FCSTD DOCUMENT  (FreeCAD 0.16R6710 (Git))
Label: body
License: All rights reserved
LicenseURL: http://en.wikipedia.org/wiki/All_rights_reserved
objects: Sketcher::SketchObject×1
note: 1 computed .brp shape members not serialized (recipe doc carries the construction recipe); baked Part::Feature solids carry a one-line shape summary decoded from their .brp

FEATURE [Sketcher::SketchObject] Sketch  label="body"
  sketch-geometry (89):
    g0: LineSegment [constr] StartX=205.497 StartY=-4.89478 StartZ=0 EndX=205.497 EndY=-171.461 EndZ=0
    g1: GeomPoint [constr] X=205.497 Y=-88.1781 Z=0
    g2: GeomPoint [constr] X=255.497 Y=-88.1781 Z=0
    g3: LineSegment StartX=258.497 StartY=-82.2781 StartZ=0 EndX=280.997 EndY=-82.2781 EndZ=0
    g4: LineSegment StartX=280.997 StartY=-82.2781 StartZ=0 EndX=280.997 EndY=-94.0781 EndZ=0
    g5: LineSegment StartX=280.997 StartY=-94.0781 StartZ=0 EndX=258.497 EndY=-94.0781 EndZ=0
    g6: LineSegment StartX=258.497 StartY=-94.0781 StartZ=0 EndX=258.497 EndY=-82.2781 EndZ=0
    g7: Circle CenterX=283.997 CenterY=-88.1781 CenterZ=0 NormalX=0 NormalY=0 NormalZ=1 Radius=1.2
    g8: Circle CenterX=255.497 CenterY=-88.1781 CenterZ=0 NormalX=0 NormalY=0 NormalZ=1 Radius=1.2
    g9: GeomPoint [constr] X=275.097 Y=-88.1781 Z=0
    g10: LineSegment [constr] StartX=135.897 StartY=-88.1781 StartZ=0 EndX=275.097 EndY=-88.1781 EndZ=0
    g11: GeomPoint [constr] X=155.497 Y=-88.1781 Z=0
    g12: LineSegment StartX=152.497 StartY=-94.0781 StartZ=0 EndX=129.997 EndY=-94.0781 EndZ=0
    g13: LineSegment StartX=129.997 StartY=-94.0781 StartZ=0 EndX=129.997 EndY=-82.2781 EndZ=0
    g14: LineSegment StartX=129.997 StartY=-82.2781 StartZ=0 EndX=152.497 EndY=-82.2781 EndZ=0
    g15: LineSegment StartX=152.497 StartY=-82.2781 StartZ=0 EndX=152.497 EndY=-94.0781 EndZ=0
    g16: Circle CenterX=126.997 CenterY=-88.1781 CenterZ=0 NormalX=0 NormalY=0 NormalZ=1 Radius=1.2
    g17: Circle CenterX=155.497 CenterY=-88.1781 CenterZ=0 NormalX=0 NormalY=0 NormalZ=1 Radius=1.2
    g18: GeomPoint [constr] X=135.897 Y=-88.1781 Z=0
    g19: GeomPoint [constr] X=205.497 Y=-31.8304 Z=0
    g20: GeomPoint [constr] X=205.497 Y=-144.526 Z=0
    g21: LineSegment [constr] StartX=205.497 StartY=-31.8304 StartZ=0 EndX=263.261 EndY=-4.89478 EndZ=0
    g22: LineSegment [constr] StartX=263.261 StartY=-4.89478 StartZ=0 EndX=147.733 EndY=-4.89478 EndZ=0
    g23: GeomPoint [constr] X=205.497 Y=-4.89478 Z=0
    g24: GeomPoint [constr] X=245.497 Y=-13.1781 Z=0
    g25: LineSegment StartX=245.723 StartY=-6.56303 StartZ=0 EndX=266.115 EndY=2.94588 EndZ=0
    g26: LineSegment StartX=266.115 StartY=2.94588 StartZ=0 EndX=271.101 EndY=-7.74855 EndZ=0
    g27: LineSegment StartX=271.101 StartY=-7.74855 StartZ=0 EndX=250.709 EndY=-17.2575 EndZ=0
    g28: LineSegment StartX=250.709 StartY=-17.2575 StartZ=0 EndX=245.723 EndY=-6.56303 EndZ=0
    g29: Circle CenterX=271.327 CenterY=-1.13348 CenterZ=0 NormalX=0 NormalY=0 NormalZ=1 Radius=1.2
    g30: Circle CenterX=245.497 CenterY=-13.1781 CenterZ=0 NormalX=0 NormalY=0 NormalZ=1 Radius=1.2
    g31: GeomPoint [constr] X=263.261 Y=-4.89478 Z=0
    g32: LineSegment [constr] StartX=205.497 StartY=-31.8304 StartZ=0 EndX=147.733 EndY=-4.89478 EndZ=0
    g33: GeomPoint [constr] X=165.497 Y=-13.1781 Z=0
    g34: LineSegment StartX=160.285 StartY=-17.2575 StartZ=0 EndX=139.893 EndY=-7.74855 EndZ=0
    g35: LineSegment StartX=139.893 StartY=-7.74855 StartZ=0 EndX=144.88 EndY=2.94588 EndZ=0
    g36: LineSegment StartX=144.88 StartY=2.94588 StartZ=0 EndX=165.272 EndY=-6.56303 EndZ=0
    g37: LineSegment StartX=165.272 StartY=-6.56303 StartZ=0 EndX=160.285 EndY=-17.2575 EndZ=0
    g38: Circle CenterX=139.667 CenterY=-1.13348 CenterZ=0 NormalX=0 NormalY=0 NormalZ=1 Radius=1.2
    g39: Circle CenterX=165.497 CenterY=-13.1781 CenterZ=0 NormalX=0 NormalY=0 NormalZ=1 Radius=1.2
    g40: GeomPoint [constr] X=147.733 Y=-4.89478 Z=0
    g41: LineSegment [constr] StartX=263.261 StartY=-4.89478 StartZ=0 EndX=263.261 EndY=-171.461 EndZ=0
    g42: GeomPoint [constr] X=263.261 Y=-88.1781 Z=0
    g43: LineSegment [constr] StartX=205.497 StartY=-144.526 StartZ=0 EndX=263.261 EndY=-171.461 EndZ=0
    g44: LineSegment [constr] StartX=205.497 StartY=-144.526 StartZ=0 EndX=147.733 EndY=-171.461 EndZ=0
    g45: LineSegment StartX=271.101 StartY=-168.608 StartZ=0 EndX=266.115 EndY=-179.302 EndZ=0
    g46: Circle CenterX=271.327 CenterY=-175.223 CenterZ=0 NormalX=0 NormalY=0 NormalZ=1 Radius=1.2
    g47: GeomPoint [constr] X=263.261 Y=-171.461 Z=0
    g48: GeomPoint [constr] X=245.497 Y=-163.178 Z=0
    g49: LineSegment StartX=250.709 StartY=-159.099 StartZ=0 EndX=271.101 EndY=-168.608 EndZ=0
    g50: LineSegment StartX=266.115 StartY=-179.302 StartZ=0 EndX=245.723 EndY=-169.793 EndZ=0
    g51: LineSegment StartX=245.723 StartY=-169.793 StartZ=0 EndX=250.709 EndY=-159.099 EndZ=0
    g52: Circle CenterX=245.497 CenterY=-163.178 CenterZ=0 NormalX=0 NormalY=0 NormalZ=1 Radius=1.2
    g53: LineSegment StartX=144.88 StartY=-179.302 StartZ=0 EndX=139.893 EndY=-168.608 EndZ=0
    g54: Circle CenterX=139.667 CenterY=-175.223 CenterZ=0 NormalX=0 NormalY=0 NormalZ=1 Radius=1.2
    g55: GeomPoint [constr] X=147.733 Y=-171.461 Z=0
    g56: GeomPoint [constr] X=165.497 Y=-163.178 Z=0
    g57: LineSegment StartX=165.272 StartY=-169.793 StartZ=0 EndX=144.88 EndY=-179.302 EndZ=0
    g58: LineSegment StartX=139.893 StartY=-168.608 StartZ=0 EndX=160.285 EndY=-159.099 EndZ=0
    g59: LineSegment StartX=160.285 StartY=-159.099 StartZ=0 EndX=165.272 EndY=-169.793 EndZ=0
    g60: Circle CenterX=165.497 CenterY=-163.178 CenterZ=0 NormalX=0 NormalY=0 NormalZ=1 Radius=1.2
    g61: ArcOfCircle CenterX=263.261 CenterY=-4.89478 CenterZ=0 NormalX=0 NormalY=0 NormalZ=1 Radius=13 StartAngle=5.14872 EndAngle=8.29031
    g62: ArcOfCircle CenterX=275.097 CenterY=-88.1781 CenterZ=0 NormalX=0 NormalY=0 NormalZ=1 Radius=13 StartAngle=4.71239 EndAngle=7.85398
    g63: LineSegment [constr] StartX=275.097 StartY=-88.1781 StartZ=0 EndX=288.683 EndY=-82.3075 EndZ=0
    g64: LineSegment [constr] StartX=288.683 StartY=-82.3075 StartZ=0 EndX=287.497 EndY=-96.2572 EndZ=0
    g65: LineSegment [constr] StartX=287.497 StartY=-96.2572 StartZ=0 EndX=275.097 EndY=-88.1781 EndZ=0
    g66: GeomPoint [constr] X=288.09 Y=-89.2824 Z=0
    g67: LineSegment [constr] StartX=275.097 StartY=-88.1781 StartZ=0 EndX=308.018 EndY=-90.976 EndZ=0
    g68: LineSegment [constr] StartX=257.767 StartY=6.88722 StartZ=0 EndX=268.755 EndY=-16.6768 EndZ=0
    g69: LineSegment [constr] StartX=275.097 StartY=-75.1781 StartZ=0 EndX=275.097 EndY=-101.178 EndZ=0
    g70: LineSegment [constr] StartX=263.261 StartY=-4.89478 StartZ=0 EndX=276.573 EndY=1.57163 EndZ=0
    g71: LineSegment [constr] StartX=276.573 StartY=1.57163 StartZ=0 EndX=276.007 EndY=-12.4169 EndZ=0
    g72: LineSegment [constr] StartX=276.007 StartY=-12.4169 StartZ=0 EndX=263.261 EndY=-4.89478 EndZ=0
    g73: GeomPoint [constr] X=276.29 Y=-5.42263 Z=0
    g74: LineSegment [constr] StartX=263.261 StartY=-4.89478 StartZ=0 EndX=296.274 EndY=-6.23222 EndZ=0
    g75: ArcOfCircle CenterX=263.261 CenterY=-171.461 CenterZ=0 NormalX=0 NormalY=0 NormalZ=1 Radius=13 StartAngle=4.27606 EndAngle=7.41765
    g76: LineSegment [constr] StartX=268.755 StartY=-159.679 StartZ=0 EndX=257.767 EndY=-183.243 EndZ=0
    g77: ArcOfCircle CenterX=147.733 CenterY=-171.461 CenterZ=0 NormalX=0 NormalY=0 NormalZ=1 Radius=13 StartAngle=2.00713 EndAngle=5.14872
    g78: ArcOfCircle CenterX=135.897 CenterY=-88.1781 CenterZ=0 NormalX=0 NormalY=0 NormalZ=1 Radius=13 StartAngle=1.5708 EndAngle=4.71239
    g79: ArcOfCircle CenterX=147.733 CenterY=-4.89478 CenterZ=0 NormalX=0 NormalY=0 NormalZ=1 Radius=13 StartAngle=1.13446 EndAngle=4.27606
    g80: LineSegment [constr] StartX=142.239 StartY=-159.679 StartZ=0 EndX=153.228 EndY=-183.243 EndZ=0
    g81: LineSegment [constr] StartX=135.897 StartY=-75.1781 StartZ=0 EndX=135.897 EndY=-101.178 EndZ=0
    g82: LineSegment [constr] StartX=153.228 StartY=6.88722 StartZ=0 EndX=142.239 EndY=-16.6768 EndZ=0
    g83: ArcOfCircle CenterX=275.098 CenterY=-45.5836 CenterZ=0 NormalX=0 NormalY=0 NormalZ=1 Radius=29.5945 StartAngle=1.78679 EndAngle=4.71238
    g84: ArcOfCircle CenterX=275.098 CenterY=-130.773 CenterZ=0 NormalX=0 NormalY=0 NormalZ=1 Radius=29.5945 StartAngle=1.57081 EndAngle=4.49639
    g85: ArcOfCircle CenterX=135.897 CenterY=-130.773 CenterZ=0 NormalX=0 NormalY=0 NormalZ=1 Radius=29.5945 StartAngle=4.92839 EndAngle=7.85397
    g86: ArcOfCircle CenterX=135.897 CenterY=-45.5836 CenterZ=0 NormalX=0 NormalY=0 NormalZ=1 Radius=29.5945 StartAngle=4.7124 EndAngle=7.63798
    g87: ArcOfCircle CenterX=205.497 CenterY=118.979 CenterZ=0 NormalX=0 NormalY=0 NormalZ=1 Radius=123.68 StartAngle=4.27606 EndAngle=5.14872
    g88: ArcOfCircle CenterX=205.497 CenterY=-295.335 CenterZ=0 NormalX=0 NormalY=0 NormalZ=1 Radius=123.68 StartAngle=1.13446 EndAngle=2.00713
  constraints (226):
    c: Vertical(g0)
    c: Symmetric(g0,g0,g1)
    c: Coincident(g3,g4)
    c: Coincident(g4,g5)
    c: Coincident(g5,g6)
    c: Coincident(g6,g3)
    c: Distance(g4,g3) = 11.8
    c: Distance(g4,g6) = 22.5
    c: Perpendicular(g6,g3)
    c: Perpendicular(g6,g5)
    c: Perpendicular(g4,g5)
    c: Distance(g7,g4) = 3
    c: Distance(g7,g3) = 5.9
    c: Distance(g8,g3) = 5.9
    c: Distance(g8,g6) = 3
    c: Coincident(g2,g8)
    c: Distance(g9,g4) = 5.9
    c: Distance(g9,g3) = 5.9
    c: Horizontal(g10)
    c: Symmetric(g10,g10,g1)
    c: Coincident(g9,g10)
    c: PointOnObject(g2,g10)
    c: Coincident(g12,g13)
    c: Coincident(g13,g14)
    c: Coincident(g14,g15)
    c: Coincident(g15,g12)
    c: Distance(g13,g12) = 11.8
    c: Distance(g13,g15) = 22.5
    c: Perpendicular(g15,g12)
    c: Perpendicular(g15,g14)
    c: Perpendicular(g13,g14)
    c: Distance(g16,g13) = 3
    c: Distance(g16,g12) = 5.9
    c: Distance(g17,g12) = 5.9
    c: Distance(g17,g15) = 3
    c: Coincident(g11,g17)
    c: Distance(g18,g13) = 5.9
    c: Distance(g18,g12) = 5.9
    c: Coincident(g10,g18)
    c: PointOnObject(g11,g10)
    c: PointOnObject(g19,g0)
    c: Symmetric(g20,g19,g1)
    c: Coincident(g21,g19)
    c: Coincident(g22,g21)
    c: Horizontal(g22)
    c: PointOnObject(g23,g22)
    c: PointOnObject(g23,g0)
    c: Symmetric(g21,g22,g23)
    c: Coincident(g25,g26)
    c: Coincident(g26,g27)
    c: Coincident(g27,g28)
    c: Coincident(g28,g25)
    c: Distance(g26,g25) = 11.8
    c: Distance(g26,g28) = 22.5
    c: Perpendicular(g28,g25)
    c: Perpendicular(g28,g27)
    c: Perpendicular(g26,g27)
    c: Distance(g29,g26) = 3
    c: Distance(g29,g25) = 5.9
    c: Distance(g30,g25) = 5.9
    c: Distance(g30,g28) = 3
    c: Coincident(g24,g30)
    c: Distance(g31,g26) = 5.9
    c: Distance(g31,g25) = 5.9
    c: Coincident(g21,g31)
    c: PointOnObject(g24,g21)
    c: Coincident(g32,g19)
    c: Coincident(g32,g22)
    c: Coincident(g34,g35)
    c: Coincident(g35,g36)
    c: Coincident(g36,g37)
    c: Coincident(g37,g34)
    c: Distance(g35,g34) = 11.8
    c: Distance(g35,g37) = 22.5
    c: Perpendicular(g37,g34)
    c: Perpendicular(g37,g36)
    c: Perpendicular(g35,g36)
    c: Distance(g38,g35) = 3
    c: Distance(g38,g34) = 5.9
    c: Distance(g39,g34) = 5.9
    c: Distance(g39,g37) = 3
    c: Coincident(g33,g39)
    c: Distance(g40,g35) = 5.9
    c: Distance(g40,g34) = 5.9
    c: Coincident(g22,g40)
    c: PointOnObject(g33,g32)
    c: Vertical(g41)
    c: Coincident(g21,g41)
    c: PointOnObject(g42,g41)
    c: PointOnObject(g42,g10)
    c: Symmetric(g21,g41,g42)
    c: PointOnObject(g0,g22)
    c: Radius(g7) = 1.2
    c: Radius(g8) = 1.2
    c: Radius(g29) = 1.2
    c: Radius(g30) = 1.2
    c: Radius(g38) = 1.2
    c: Radius(g39) = 1.2
    c: Radius(g17) = 1.2
    c: Radius(g16) = 1.2
    c: Coincident(g43,g20)
    c: Coincident(g43,g41)
    c: Coincident(g44,g20)
    c: Symmetric(g41,g44,g0)
    c: Coincident(g49,g45)
    c: Coincident(g45,g50)
    c: Coincident(g50,g51)
    c: Coincident(g51,g49)
    c: Distance(g45,g49) = 11.8
    c: Distance(g45,g51) = 22.5
    c: Perpendicular(g51,g49)
    c: Perpendicular(g51,g50)
    c: Perpendicular(g45,g50)
    c: Distance(g46,g45) = 3
    c: Distance(g46,g49) = 5.9
    c: Distance(g52,g49) = 5.9
    c: Distance(g52,g51) = 3
    c: Coincident(g48,g52)
    c: Distance(g47,g45) = 5.9
    c: Distance(g47,g49) = 5.9
    c: Equal(g7,g46) = 1.2
    c: Equal(g8,g52) = 1.2
    c: Coincident(g41,g47)
    c: PointOnObject(g48,g43)
    c: Coincident(g57,g53)
    c: Coincident(g53,g58)
    c: Coincident(g58,g59)
    c: Coincident(g59,g57)
    c: Distance(g53,g57) = 11.8
    c: Distance(g53,g59) = 22.5
    c: Perpendicular(g59,g57)
    c: Perpendicular(g59,g58)
    c: Perpendicular(g53,g58)
    c: Distance(g54,g53) = 3
    c: Distance(g54,g57) = 5.9
    c: Distance(g60,g57) = 5.9
    c: Distance(g60,g59) = 3
    c: Coincident(g56,g60)
    c: Distance(g55,g53) = 5.9
    c: Distance(g55,g57) = 5.9
    c: Coincident(g44,g55)
    c: PointOnObject(g56,g44)
    c: Radius(g54) = 1.2
    c: Radius(g60) = 1.2
    c: Angle(g10,g21) = 0.436332
    c: Distance(g33,g24) = 80
    c: Distance(g48,g24) = 150
    c: Distance(g11,g2) = 100
    c: Coincident(g61,g21)
    c: Radius(g61) = 13
    c: Coincident(g62,g9)
    c: Radius(g62) = 13
    c: Coincident(g64,g63)
    c: Coincident(g64,g65)
    c: Coincident(g63,g65)
    c: Coincident(g9,g63)
    c: Distance(g9,g64) = 14.8
    c: Distance(g9,g63) = 14.8
    c: Distance(g64,g63) = 14
    c: DistanceX(g1) = 205.497
    c: DistanceY(g1) = -88.1781
    c: Symmetric(g63,g64,g66)
    c: Coincident(g67,g9)
    c: PointOnObject(g66,g67)
    c: Distance(g66,g67) = 20
    c: Coincident(g68,g61)
    c: Coincident(g68,g61)
    c: PointOnObject(g21,g68)
    c: Perpendicular(g68,g21)
    c: Coincident(g69,g62)
    c: Coincident(g69,g62)
    c: PointOnObject(g9,g69)
    c: Perpendicular(g69,g10)
    c: Coincident(g70,g21)
    c: Coincident(g71,g70)
    c: Coincident(g72,g71)
    c: Coincident(g72,g21)
    c: Distance(g71,g21) = 14.8
    c: Distance(g21,g70) = 14.8
    c: Distance(g70,g71) = 14
    c: Symmetric(g70,g71,g73)
    c: Coincident(g74,g21)
    c: PointOnObject(g73,g74)
    c: Distance(g74,g73) = 20
    c: Coincident(g75,g41)
    c: Radius(g75) = 13
    c: Coincident(g76,g75)
    c: Coincident(g76,g75)
    c: PointOnObject(g41,g76)
    c: Perpendicular(g76,g43)
    c: Coincident(g77,g44)
    c: Coincident(g78,g10)
    c: Coincident(g79,g22)
    c: Radius(g79) = 13
    c: Radius(g78) = 13
    c: Radius(g77) = 13
    c: Coincident(g80,g77)
    c: Coincident(g80,g77)
    c: PointOnObject(g44,g80)
    c: Perpendicular(g44,g80)
    c: Coincident(g81,g78)
    c: Coincident(g81,g78)
    c: PointOnObject(g10,g81)
    c: Perpendicular(g10,g81)
    c: Coincident(g82,g79)
    c: Coincident(g82,g79)
    c: PointOnObject(g22,g82)
    c: Perpendicular(g32,g82)
    c: Coincident(g83,g61)
    c: Coincident(g83,g62)
    c: Coincident(g84,g62)
    c: Coincident(g75,g84)
    c: Radius(g83) = 29.5945
    c: Radius(g84) = 29.5945
    c: Coincident(g85,g78)
    c: Coincident(g77,g85)
    c: Radius(g85) = 29.5945
    c: Coincident(g86,g79)
    c: Coincident(g86,g78)
    c: Radius(g86) = 29.5945
    c: Coincident(g87,g79)
    c: Coincident(g87,g61)
    c: Coincident(g88,g77)
    c: Coincident(g88,g75)
    c: Radius(g88) = 123.68
    c: Radius(g87) = 123.68
